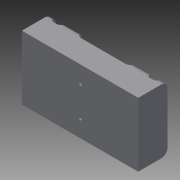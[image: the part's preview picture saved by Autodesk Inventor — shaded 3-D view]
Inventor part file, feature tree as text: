
AUTODESK INVENTOR PART (.ipt)
format: ipt  version: 2014 (Build 180170000, 170)  size: 231,936 bytes
history: native  units: mm
features: sketch x6, extrude x4, other x2, plane x1, fillet x1, shell x1, mirror x1, hole x1, projected_geometry x1
ambient origin geometry x8: Origin, YZ Plane, XZ Plane, XY Plane, X Axis, Y Axis, Z Axis, Center Point
bodies: Volumenkörper1 (feature_tree)
feature tree (18):
  extrude  "Extrusion1"  Depth=4.0mm
  plane  "Arbeitsebene1"
  fillet  "Rundung2"  Radius=19.0mm
  shell  "Hülle1"  Thickness=4.0mm
  extrude  "Extrusion2"  Depth=2.0mm
  mirror  "Spiegeln1"
  extrude  "Extrusion3"  Depth=2.0mm
  extrude  "Extrusion4"  Depth=2.0mm
  hole  "Bohrung2"  [1 undecoded]
  sketch  "Skizze5"  dims[d13=2.0mm d14=2.0mm]
  other  "Arbeitsachse1"
  other  "Arbeitsachse2"
  sketch  "Skizze1"  dims[d0=75.5mm d1=41.5mm d2=19.0mm d3=0.0mm d4=4.0mm]
  sketch  "Skizze2"  dims[d5=2.0mm d6=2.0mm]
  sketch  "Skizze3"  dims[d7=2.0mm d8=2.0mm]
  sketch  "Skizze4"  dims[d9=19.0mm d10=0.0mm d12=2.0mm]
  sketch  "Skizze7"  dims[d15=4.0mm d16=4.0mm d17=19.0mm d18=0.0mm d19=4.0mm d20=1.5mm d21=19.0mm d22=0.0mm d32=2.0mm d33=6.0mm d34=4.0mm d35=0.25mm d36=90.0deg d37=8.0mm d38=20.594885mm]
  projected_geometry  "Projizierte Kontur1"
note: 1 required parameter value undecoded (feature->parameter linkage not recoverable at this tier; creation-order binding heuristic only, values carry confidence <= 0.55)
